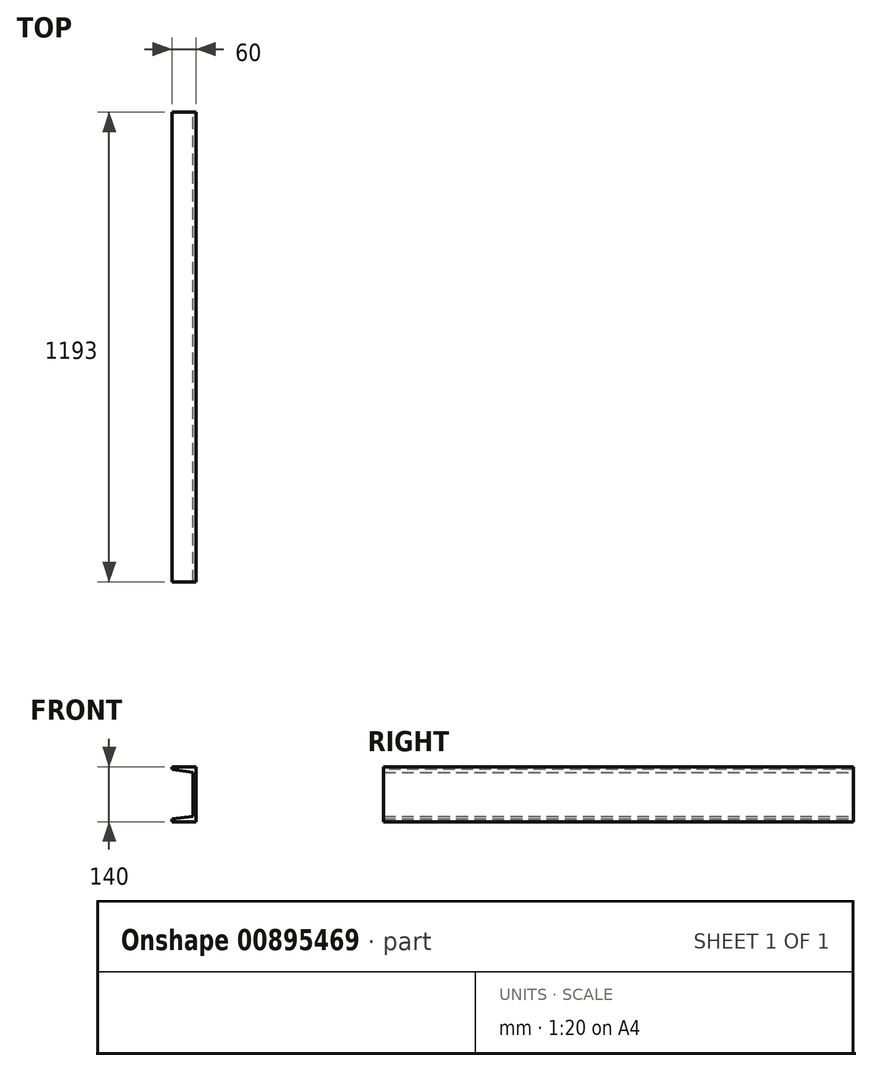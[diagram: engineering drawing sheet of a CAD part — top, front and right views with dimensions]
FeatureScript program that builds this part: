
annotation { "Feature Type Name" : "Feature", "Feature Type Description" : "" }
export const myFeature = defineFeature(function(context is Context, id is Id, definition is map)
    precondition{}
    {
        {
            var Q0;
            Q0=qCreatedBy(makeId("Front.planeOp"),FACE);
            var sketch = newSketch(context, id + "F0", { "sketchPlane" : qUnion([Q0])});
            skLineSegment(sketch, "E0", {"start": v(0, 0) * mm, "end": v(0, 140) * mm});
            skLineSegment(sketch, "E1", {"start": v(0, 140) * mm, "end": v(-60, 140) * mm});
            skLineSegment(sketch, "E2", {"start": v(-60, 140) * mm, "end": v(-60, 126) * mm});
            skLineSegment(sketch, "E3", {"start": v(-60, 126) * mm, "end": v(-7, 126) * mm});
            skLineSegment(sketch, "E4", {"start": v(-7, 126) * mm, "end": v(-7, 14) * mm});
            skLineSegment(sketch, "E5", {"start": v(-7, 14) * mm, "end": v(-60, 14) * mm});
            skLineSegment(sketch, "E6", {"start": v(-60, 14) * mm, "end": v(-60, 0) * mm});
            skLineSegment(sketch, "E7", {"start": v(-60, 0) * mm, "end": v(0, 0) * mm});
            skSolve(sketch);
        }
        {
            var Q0;
            Q0 = qSketchRegion(id + "F0", true);
            extrude(context, id + "F1", {"entities" : qUnion([Q0]), "endBound" : BoundingType.SYMMETRIC, "depth" : 1193 * mm, "offsetDistance" : 25 * mm});
        }
        {
            var Q0;
            Q0=makeQuery(id+"F1.opExtrude","SWEPT_EDGE",EDGE,{"disambiguationData":[OSD([sQuery(id+"F0.wireOp",EDGE,"E5"),sQuery(id+"F0.wireOp",EDGE,"E6")])]});
            chamfer(context, id + "F2", {"entities" : qUnion([Q0]), "chamferType" : ChamferType.TWO_OFFSETS, "width1" : 7 * mm, "oppositeDirection" : false, "width2" : 53 * mm, "tangentPropagation" : true});
        }
        {
            var Q0;
            Q0=makeQuery(id+"F1.opExtrude","SWEPT_EDGE",EDGE,{"disambiguationData":[OSD([sQuery(id+"F0.wireOp",EDGE,"E2"),sQuery(id+"F0.wireOp",EDGE,"E3")])]});
            chamfer(context, id + "F3", {"entities" : qUnion([Q0]), "chamferType" : ChamferType.TWO_OFFSETS, "width1" : 53 * mm, "oppositeDirection" : false, "width2" : 7 * mm, "tangentPropagation" : true});
        }
    });
